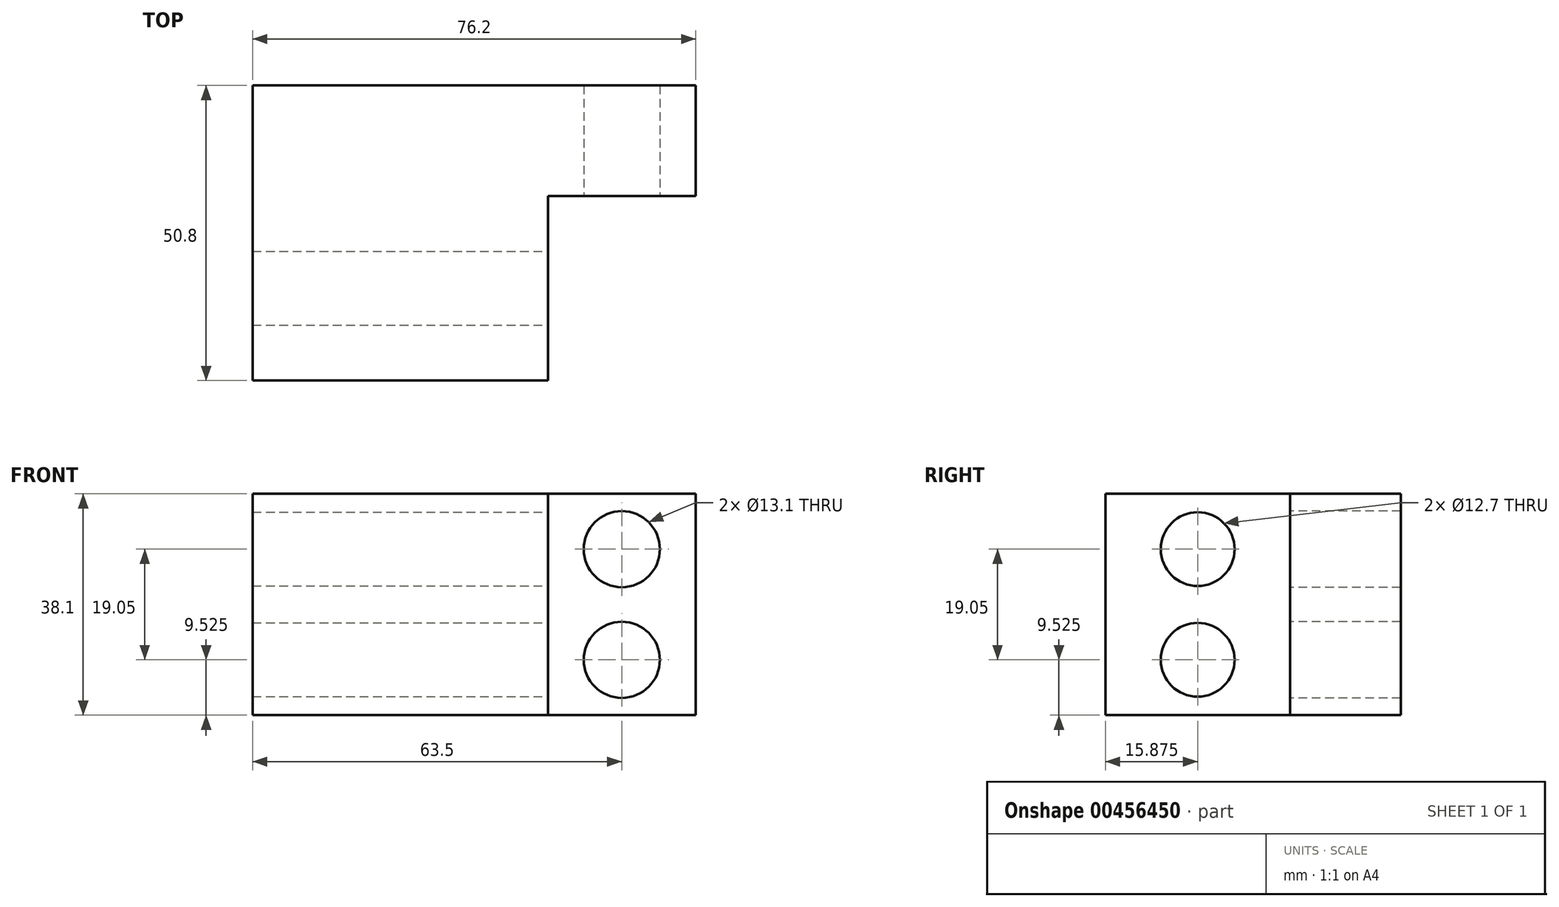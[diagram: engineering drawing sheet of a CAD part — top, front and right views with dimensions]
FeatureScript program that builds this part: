
annotation { "Feature Type Name" : "Feature", "Feature Type Description" : "" }
export const myFeature = defineFeature(function(context is Context, id is Id, definition is map)
    precondition{}
    {
        {
            var Q0;
            Q0=qCreatedBy(makeId("Front.planeOp"),FACE);
            var sketch = newSketch(context, id + "F0", { "sketchPlane" : qUnion([Q0])});
            skLineSegment(sketch, "E0.bottom", {"start": v(38.1, -19.05) * mm, "end": v(-38.1, -19.05) * mm});
            skLineSegment(sketch, "E0.top", {"start": v(38.1, 19.05) * mm, "end": v(-38.1, 19.05) * mm});
            skLineSegment(sketch, "E0.left", {"start": v(38.1, -19.05) * mm, "end": v(38.1, 19.05) * mm});
            skLineSegment(sketch, "E0.right", {"start": v(-38.1, -19.05) * mm, "end": v(-38.1, 19.05) * mm});
            skPoint(sketch, "E0.middle", {"position": v(0, 0) * mm});
            skLineSegment(sketch, "E1", {"start": v(12.7, 19.05) * mm, "end": v(12.7, -19.05) * mm});
            skLineSegment(sketch, "E2", {"start": v(25.4, 19.05) * mm, "end": v(25.4, -19.05) * mm});
            skLineSegment(sketch, "E3", {"start": v(38.1, 9.53) * mm, "end": v(12.7, 9.53) * mm});
            skLineSegment(sketch, "E4", {"start": v(38.1, -9.52) * mm, "end": v(12.7, -9.52) * mm});
            skPoint(sketch, "E4.endSnap0", {"position": v(12.7, 0) * mm});
            skSolve(sketch);
        }
        {
            var Q0;
            Q0 = qSketchRegion(id + "F0", true);
            var Q1;
            {var subQ0=sQuery(id+"F0.wireOp",EDGE,"E3");var subQ1=sQuery(id+"F0.wireOp",EDGE,"E1");var subQ2=makeQuery(id+"F0.imprint","INTERSECT",VERTEX,{"derivedFrom":[subQ1,subQ0]});Q1=makeQuery(id+"F0.imprint","IMPRINT",FACE,{"disambiguationData":[TD([[makeQuery(id+"F0.imprint","IMPRINT",EDGE,{"disambiguationData":[TD([[subQ2,-1.0]])],"derivedFrom":subQ1}),1.0]])]});}
            extrude(context, id + "F1", {"entities" : qUnion([Q0, Q1]), "endBound" : BoundingType.SYMMETRIC, "depth" : 50.8 * mm});
        }
        {
            var Q0;
            Q0=makeQuery(id+"F1.opExtrude","SWEPT_FACE",FACE,{"disambiguationData":[OSD([sQuery(id+"F0.wireOp",EDGE,"E0.top")])]});
            var sketch = newSketch(context, id + "F2", { "sketchPlane" : qUnion([Q0])});
            skLineSegment(sketch, "E5.bottom", {"start": v(38.1, -25.4) * mm, "end": v(12.7, -25.4) * mm});
            skLineSegment(sketch, "E5.top", {"start": v(38.1, 6.35) * mm, "end": v(12.7, 6.35) * mm});
            skLineSegment(sketch, "E5.left", {"start": v(38.1, -25.4) * mm, "end": v(38.1, 6.35) * mm});
            skLineSegment(sketch, "E5.right", {"start": v(12.7, -25.4) * mm, "end": v(12.7, 6.35) * mm});
            skSolve(sketch);
        }
        {
            var Q0;
            Q0 = qSketchRegion(id + "F2", true);
            extrude(context, id + "F3", {"entities" : qUnion([Q0]), "operationType" : NewBodyOperationType.REMOVE, "endBound" : BoundingType.THROUGH_ALL, "oppositeDirection" : true, "depth" : 25.4 * mm});
        }
        {
            var Q0;
            Q0=makeQuery(id+"F3.boolean.opBoolean","COPY",FACE,{"derivedFrom":makeQuery(id+"F3.opExtrude","SWEPT_FACE",FACE,{"disambiguationData":[OSD([sQuery(id+"F2.wireOp",EDGE,"E5.top")])]})});
            var sketch = newSketch(context, id + "F4", { "sketchPlane" : qUnion([Q0])});
            skLineSegment(sketch, "E6", {"start": v(25.4, 19.05) * mm, "end": v(25.4, -19.05) * mm});
            skLineSegment(sketch, "E7", {"start": v(38.1, 9.53) * mm, "end": v(12.7, 9.53) * mm});
            skLineSegment(sketch, "E8", {"start": v(38.1, -9.52) * mm, "end": v(12.7, -9.52) * mm});
            skCircle(sketch, "E9", {"center": v(25.4, 9.53) * mm, "radius": 6.55 * mm});
            skCircle(sketch, "E10", {"center": v(25.4, -9.52) * mm, "radius": 6.55 * mm});
            skSolve(sketch);
        }
        {
            var Q0;
            Q0 = qSketchRegion(id + "F4", true);
            extrude(context, id + "F5", {"entities" : qUnion([Q0]), "operationType" : NewBodyOperationType.REMOVE, "endBound" : BoundingType.THROUGH_ALL, "oppositeDirection" : true, "depth" : 25.4 * mm});
        }
        {
            var Q0;
            Q0=makeQuery(id+"F3.boolean.opBoolean","COPY",FACE,{"derivedFrom":makeQuery(id+"F3.opExtrude","SWEPT_FACE",FACE,{"disambiguationData":[OSD([sQuery(id+"F2.wireOp",EDGE,"E5.right")])]})});
            var sketch = newSketch(context, id + "F6", { "sketchPlane" : qUnion([Q0])});
            skLineSegment(sketch, "E11", {"start": v(-9.53, 19.05) * mm, "end": v(-9.53, -19.05) * mm});
            skLineSegment(sketch, "E12", {"start": v(-25.4, 9.53) * mm, "end": v(6.35, 9.53) * mm});
            skLineSegment(sketch, "E13", {"start": v(-25.4, -9.52) * mm, "end": v(6.35, -9.52) * mm});
            skPoint(sketch, "E14", {"position": v(-9.53, 9.53) * mm});
            skPoint(sketch, "E15", {"position": v(-9.53, -9.52) * mm});
            skCircle(sketch, "E16", {"center": v(-9.53, 9.53) * mm, "radius": 6.35 * mm});
            skCircle(sketch, "E17", {"center": v(-9.53, -9.52) * mm, "radius": 6.35 * mm});
            skSolve(sketch);
        }
        {
            var Q0;
            Q0 = qSketchRegion(id + "F6", true);
            extrude(context, id + "F7", {"entities" : qUnion([Q0]), "operationType" : NewBodyOperationType.REMOVE, "endBound" : BoundingType.THROUGH_ALL, "oppositeDirection" : true, "depth" : 25.4 * mm});
        }
    });
